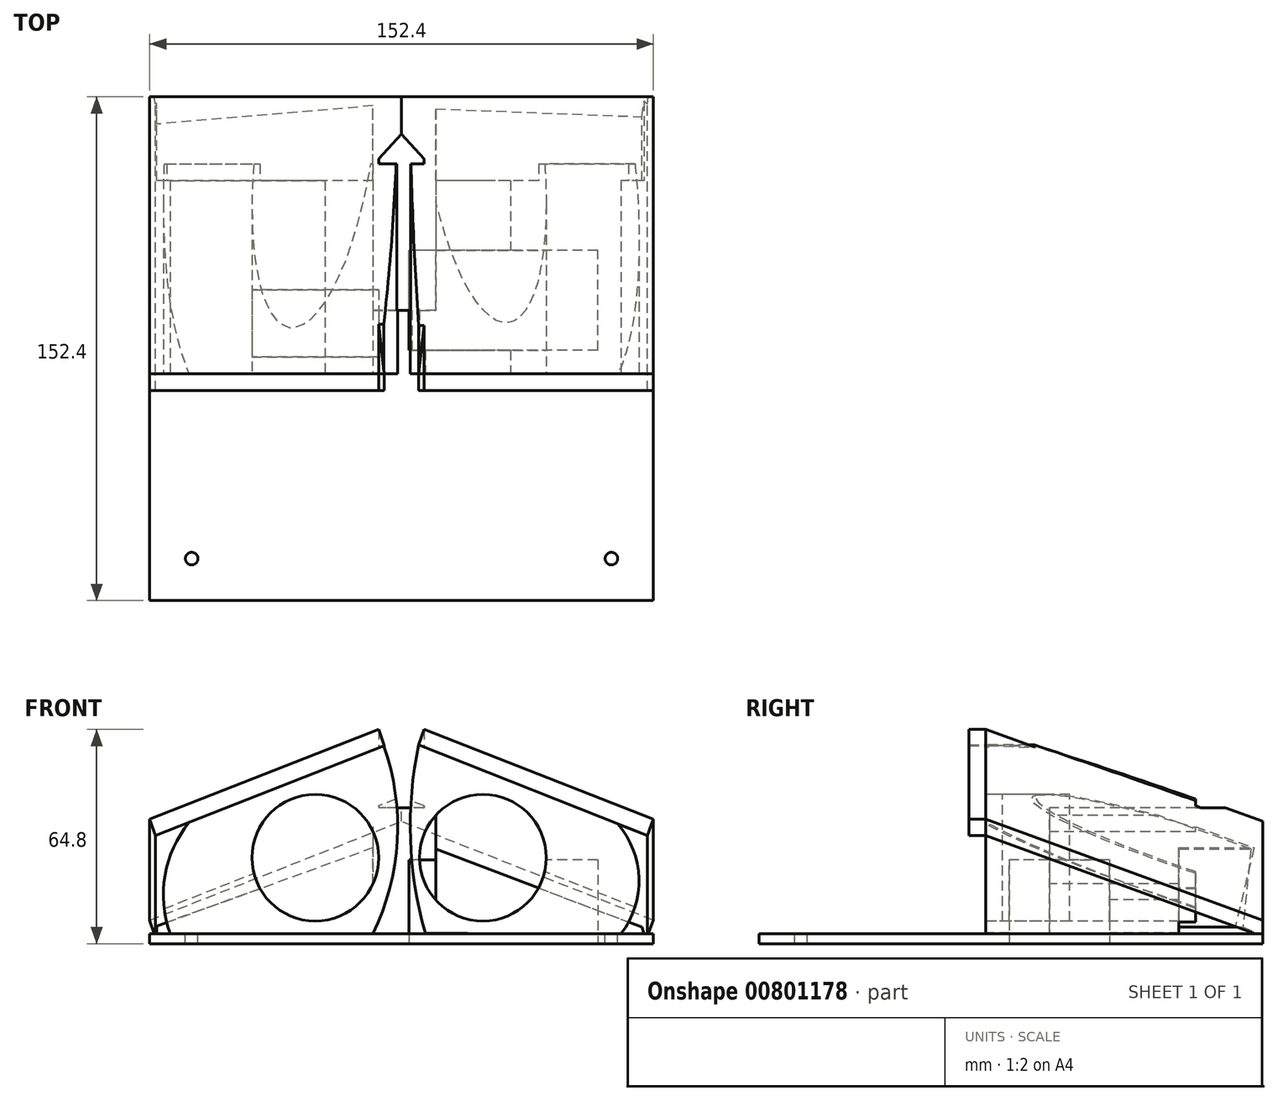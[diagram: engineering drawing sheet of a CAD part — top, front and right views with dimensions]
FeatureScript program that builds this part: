
annotation { "Feature Type Name" : "Feature", "Feature Type Description" : "" }
export const myFeature = defineFeature(function(context is Context, id is Id, definition is map)
    precondition{}
    {
        {
            var Q0;
            Q0=qCreatedBy(makeId("Top.planeOp"),FACE);
            var sketch = newSketch(context, id + "F0", { "sketchPlane" : qUnion([Q0])});
            skLineSegment(sketch, "E0.bottom", {"start": v(0, 0) * mm, "end": v(152.4, 0) * mm});
            skLineSegment(sketch, "E0.top", {"start": v(0, 152.4) * mm, "end": v(152.4, 152.4) * mm});
            skLineSegment(sketch, "E0.left", {"start": v(0, 0) * mm, "end": v(0, 152.4) * mm});
            skLineSegment(sketch, "E0.right", {"start": v(152.4, 0) * mm, "end": v(152.4, 152.4) * mm});
            skSolve(sketch);
        }
        {
            var Q0;
            Q0=makeQuery(id+"F0.imprint","IMPRINT",FACE,{"disambiguationData":[TD([[makeQuery(id+"F0.imprint","IMPRINT",EDGE,{"derivedFrom":sQuery(id+"F0.wireOp",EDGE,"E0.bottom")}),1.0]])]});
            extrude(context, id + "F1", {"entities" : qUnion([Q0]), "depth" : 3 * mm, "offsetDistance" : 25.4 * mm});
        }
        {
            var Q0;
            Q0=makeQuery(id+"F1.opExtrude","CAP_EDGE",EDGE,{"disambiguationData":[OSD([sQuery(id+"F0.wireOp",EDGE,"E0.top")])],"isStart":false});
            cPlane(context, id + "F2", {"entities" : qUnion([Q0]), "cplaneType" : CPlaneType.LINE_ANGLE, "offset" : 25.4 * mm, "angle" : 20 * degree, "oppositeDirection" : true, "width" : 152.4 * mm, "height" : 152.4 * mm});
        }
        {
            var Q0;
            Q0=qCreatedBy(id+"F2.planeOp",FACE);
            var sketch = newSketch(context, id + "F3", { "sketchPlane" : qUnion([Q0])});
            skLineSegment(sketch, "E1", {"start": v(-1.71, 54.15) * mm, "end": v(-70.98, 79.7) * mm});
            skLineSegment(sketch, "E2", {"start": v(-70.98, 79.7) * mm, "end": v(-69.27, 84.35) * mm});
            skLineSegment(sketch, "E3", {"start": v(-69.27, 84.35) * mm, "end": v(0, 58.8) * mm});
            skLineSegment(sketch, "E4", {"start": v(0, 58.8) * mm, "end": v(-1.71, 54.15) * mm});
            skLineSegment(sketch, "E5", {"start": v(0, 51.14) * mm, "end": v(-152.3, 51.14) * mm});
            skLineSegment(sketch, "E6", {"start": v(-76.15, 51.14) * mm, "end": v(-76.15, 93.23) * mm});
            skLineSegment(sketch, "E7.MirrorCS", {"start": v(-150.6, 54.15) * mm, "end": v(-81.32, 79.7) * mm});
            skLineSegment(sketch, "E8.MirrorCS", {"start": v(-83.04, 84.35) * mm, "end": v(-152.3, 58.8) * mm});
            skLineSegment(sketch, "E9.MirrorCS", {"start": v(-81.32, 79.7) * mm, "end": v(-83.04, 84.35) * mm});
            skLineSegment(sketch, "E10.MirrorCS", {"start": v(-152.3, 58.8) * mm, "end": v(-150.6, 54.15) * mm});
            skSolve(sketch);
        }
        {
            var Q0;
            Q0=makeQuery(id+"F3.imprint","IMPRINT",FACE,{"disambiguationData":[TD([[makeQuery(id+"F3.imprint","IMPRINT",EDGE,{"derivedFrom":sQuery(id+"F3.wireOp",EDGE,"E1")}),-1.0]])]});
            var Q1;
            Q1=makeQuery(id+"F3.imprint","IMPRINT",FACE,{"disambiguationData":[TD([[makeQuery(id+"F3.imprint","IMPRINT",EDGE,{"derivedFrom":sQuery(id+"F3.wireOp",EDGE,"E7.MirrorCS")}),1.0]])]});
            extrude(context, id + "F4", {"entities" : qUnion([Q0, Q1]), "operationType" : NewBodyOperationType.ADD, "oppositeDirection" : true, "depth" : 101.6 * mm, "offsetDistance" : 25.4 * mm});
        }
        {
            var Q0;
            Q0=makeQuery(id+"F1.opExtrude","SWEPT_FACE",FACE,{"disambiguationData":[OSD([sQuery(id+"F0.wireOp",EDGE,"E0.bottom")])]});
            cPlane(context, id + "F5", {"entities" : qUnion([Q0]), "cplaneType" : CPlaneType.OFFSET, "offset" : 68.58 * mm, "oppositeDirection" : true, "width" : 152.4 * mm, "height" : 152.4 * mm});
        }
        {
            var Q0;
            Q0=makeQuery(id+"F1.opExtrude","SWEPT_FACE",FACE,{"disambiguationData":[OSD([sQuery(id+"F0.wireOp",EDGE,"E0.top")])]});
            cPlane(context, id + "F6", {"entities" : qUnion([Q0]), "cplaneType" : CPlaneType.OFFSET, "offset" : 0 * mm, "width" : 152.4 * mm, "height" : 152.4 * mm});
        }
        {
            var Q0;
            Q0=qCreatedBy(id+"F6.planeOp",FACE);
            var sketch = newSketch(context, id + "F7", { "sketchPlane" : qUnion([Q0])});
            skLineSegment(sketch, "E11.bottom", {"start": v(-167.5, 48.25) * mm, "end": v(7.13, 48.25) * mm});
            skLineSegment(sketch, "E11.top", {"start": v(-167.5, -23.65) * mm, "end": v(7.13, -23.65) * mm});
            skLineSegment(sketch, "E11.left", {"start": v(-167.5, 48.25) * mm, "end": v(-167.5, -23.65) * mm});
            skLineSegment(sketch, "E11.right", {"start": v(7.13, 48.25) * mm, "end": v(7.13, -23.65) * mm});
            skSolve(sketch);
        }
        {
            var Q0;
            Q0=makeQuery(id+"F7.imprint","IMPRINT",FACE,{"disambiguationData":[TD([[makeQuery(id+"F7.imprint","IMPRINT",EDGE,{"derivedFrom":sQuery(id+"F7.wireOp",EDGE,"E11.bottom")}),-1.0]])]});
            extrude(context, id + "F8", {"entities" : qUnion([Q0]), "operationType" : NewBodyOperationType.REMOVE, "depth" : 25.4 * mm, "offsetDistance" : 25.4 * mm});
        }
        {
            var Q0;
            Q0=qCreatedBy(id+"F5.planeOp",FACE);
            var sketch = newSketch(context, id + "F9", { "sketchPlane" : qUnion([Q0])});
            skLineSegment(sketch, "E12.bottom", {"start": v(-28, 78.49) * mm, "end": v(162.26, 78.49) * mm});
            skLineSegment(sketch, "E12.top", {"start": v(-28, 8.9) * mm, "end": v(162.26, 8.9) * mm});
            skLineSegment(sketch, "E12.left", {"start": v(-28, 78.49) * mm, "end": v(-28, 8.9) * mm});
            skLineSegment(sketch, "E12.right", {"start": v(162.26, 78.49) * mm, "end": v(162.26, 8.9) * mm});
            skSolve(sketch);
        }
        {
            var Q0;
            Q0=makeQuery(id+"F9.imprint","IMPRINT",FACE,{"disambiguationData":[TD([[makeQuery(id+"F9.imprint","IMPRINT",EDGE,{"derivedFrom":sQuery(id+"F9.wireOp",EDGE,"E12.bottom")}),-1.0]])]});
            extrude(context, id + "F10", {"entities" : qUnion([Q0]), "operationType" : NewBodyOperationType.REMOVE, "depth" : 25.4 * mm, "offsetDistance" : 25.4 * mm});
        }
        {
            var Q0;
            Q0=qCreatedBy(id+"F5.planeOp",FACE);
            var sketch = newSketch(context, id + "F11", { "sketchPlane" : qUnion([Q0])});
            skCircle(sketch, "E13", {"center": v(50.1, 26.01) * mm, "radius": 19.17 * mm});
            skCircle(sketch, "E14", {"center": v(100.82, 26.01) * mm, "radius": 19.17 * mm});
            skArc(sketch, "E15", {"start": v(67.55, 2.96) * mm, "mid": v(74.9, 31.12) * mm, "end": v(70.85, 59.94) * mm});
            skArc(sketch, "E16", {"start": v(81.38, 60.1) * mm, "mid": v(78.93, 31.58) * mm, "end": v(83.35, 3.28) * mm});
            skArc(sketch, "E17", {"start": v(12.38, 37.21) * mm, "mid": v(4.68, 21) * mm, "end": v(6.13, 3.12) * mm});
            skArc(sketch, "E18", {"start": v(142.32, 2.63) * mm, "mid": v(148.07, 20) * mm, "end": v(141, 36.88) * mm});
            skLineSegment(sketch, "E19", {"start": v(6.13, 3.12) * mm, "end": v(67.55, 2.96) * mm});
            skLineSegment(sketch, "E20", {"start": v(83.35, 3.28) * mm, "end": v(142.32, 2.63) * mm});
            skLineSegment(sketch, "E21", {"start": v(81.38, 60.1) * mm, "end": v(141, 36.88) * mm});
            skLineSegment(sketch, "E22", {"start": v(70.85, 59.94) * mm, "end": v(12.38, 37.21) * mm});
            skSolve(sketch);
        }
        {
            var Q0;
            Q0=makeQuery(id+"F11.imprint","IMPRINT",FACE,{"disambiguationData":[TD([[makeQuery(id+"F11.imprint","IMPRINT",EDGE,{"derivedFrom":sQuery(id+"F11.wireOp",EDGE,"E13")}),-1.0]])]});
            var Q1;
            Q1=makeQuery(id+"F11.imprint","IMPRINT",FACE,{"disambiguationData":[TD([[makeQuery(id+"F11.imprint","IMPRINT",EDGE,{"derivedFrom":sQuery(id+"F11.wireOp",EDGE,"E14")}),-1.0]])]});
            extrude(context, id + "F12", {"entities" : qUnion([Q0, Q1]), "operationType" : NewBodyOperationType.ADD, "oppositeDirection" : true, "depth" : 63.5 * mm, "offsetDistance" : 25.4 * mm});
        }
        {
            var Q0;
            Q0=makeQuery(id+"F4.opExtrude","SWEPT_FACE",FACE,{"disambiguationData":[OSD([sQuery(id+"F3.wireOp",EDGE,"E8.MirrorCS")])]});
            var sketch = newSketch(context, id + "F13", { "sketchPlane" : qUnion([Q0])});
            skLineSegment(sketch, "E23.bottom", {"start": v(48.73, 42.28) * mm, "end": v(122.55, 42.28) * mm});
            skLineSegment(sketch, "E23.top", {"start": v(48.73, 140.78) * mm, "end": v(122.55, 140.78) * mm});
            skLineSegment(sketch, "E23.left", {"start": v(48.73, 42.28) * mm, "end": v(48.73, 140.78) * mm});
            skLineSegment(sketch, "E23.right", {"start": v(122.55, 42.28) * mm, "end": v(122.55, 140.78) * mm});
            skSolve(sketch);
        }
        {
            var Q0;
            Q0=makeQuery(id+"F4.opExtrude","SWEPT_FACE",FACE,{"disambiguationData":[OSD([sQuery(id+"F3.wireOp",EDGE,"E3")])]});
            var sketch = newSketch(context, id + "F14", { "sketchPlane" : qUnion([Q0])});
            skLineSegment(sketch, "E24.bottom", {"start": v(20.35, 140.78) * mm, "end": v(162.55, 140.78) * mm});
            skLineSegment(sketch, "E24.top", {"start": v(20.35, 0) * mm, "end": v(162.55, 0) * mm});
            skLineSegment(sketch, "E24.left", {"start": v(20.35, 140.78) * mm, "end": v(20.35, 0) * mm});
            skLineSegment(sketch, "E24.right", {"start": v(162.55, 140.78) * mm, "end": v(162.55, 0) * mm});
            skSolve(sketch);
        }
        {
            var Q0;
            Q0=makeQuery(id+"F19.boolean.opBoolean","MERGE",FACE,{"derivedFrom":[makeQuery(id+"F4.opExtrude","SWEPT_FACE",FACE,{"disambiguationData":[OSD([sQuery(id+"F3.wireOp",EDGE,"E8.MirrorCS")])]}),makeQuery(id+"F19.opExtrude","CAP_FACE",FACE,{"disambiguationData":[OSD([sQuery(id+"F13.wireOp",EDGE,"E23.bottom"),sQuery(id+"F13.wireOp",EDGE,"E23.top"),sQuery(id+"F13.wireOp",EDGE,"E23.left"),sQuery(id+"F13.wireOp",EDGE,"E23.right")])],"isStart":true})]});
            var sketch = newSketch(context, id + "F15", { "sketchPlane" : qUnion([Q0])});
            skLineSegment(sketch, "E25.bottom", {"start": v(92.17, 120.01) * mm, "end": v(2.78, 120.01) * mm});
            skLineSegment(sketch, "E25.top", {"start": v(92.17, 34.87) * mm, "end": v(2.78, 34.87) * mm});
            skLineSegment(sketch, "E25.left", {"start": v(92.17, 120.01) * mm, "end": v(92.17, 34.87) * mm});
            skLineSegment(sketch, "E25.right", {"start": v(2.78, 120.01) * mm, "end": v(2.78, 34.87) * mm});
            skSolve(sketch);
        }
        {
            var Q0;
            Q0=makeQuery(id+"F1.opExtrude","CAP_FACE",FACE,{"disambiguationData":[OSD([sQuery(id+"F0.wireOp",EDGE,"E0.bottom"),sQuery(id+"F0.wireOp",EDGE,"E0.top"),sQuery(id+"F0.wireOp",EDGE,"E0.left"),sQuery(id+"F0.wireOp",EDGE,"E0.right")])],"isStart":false});
            var sketch = newSketch(context, id + "F16", { "sketchPlane" : qUnion([Q0])});
            skLineSegment(sketch, "E26.bottom", {"start": v(67.57, 152.4) * mm, "end": v(86.52, 152.4) * mm});
            skLineSegment(sketch, "E26.top", {"start": v(67.57, 87.8) * mm, "end": v(86.52, 87.8) * mm});
            skLineSegment(sketch, "E26.left", {"start": v(67.57, 152.4) * mm, "end": v(67.57, 87.8) * mm});
            skLineSegment(sketch, "E26.right", {"start": v(86.52, 152.4) * mm, "end": v(86.52, 87.8) * mm});
            skSolve(sketch);
        }
        {
            var Q0;
            Q0 = qSketchRegion(id + "F16", true);
            extrude(context, id + "F17", {"entities" : qUnion([Q0]), "operationType" : NewBodyOperationType.ADD, "depth" : 38.1 * mm, "offsetDistance" : 25.4 * mm});
        }
        {
            var Q0;
            Q0 = qSketchRegion(id + "F14", true);
            extrude(context, id + "F18", {"entities" : qUnion([Q0]), "operationType" : NewBodyOperationType.REMOVE, "depth" : 25.4 * mm, "offsetDistance" : 25.4 * mm});
        }
        {
            var Q0;
            Q0 = qSketchRegion(id + "F13", true);
            extrude(context, id + "F19", {"entities" : qUnion([Q0]), "operationType" : NewBodyOperationType.REMOVE, "depth" : 25.4 * mm, "offsetDistance" : 25.4 * mm});
        }
        {
            var Q0;
            Q0 = qSketchRegion(id + "F15", true);
            extrude(context, id + "F20", {"entities" : qUnion([Q0]), "operationType" : NewBodyOperationType.REMOVE, "depth" : 25.4 * mm, "offsetDistance" : 25.4 * mm});
        }
        {
            var Q0;
            {var subQ7=makeQuery(id+"F4.opExtrude","SWEPT_FACE",FACE,{"disambiguationData":[OSD([sQuery(id+"F3.wireOp",EDGE,"E8.MirrorCS")])]});var subQ9=sQuery(id+"F16.wireOp",EDGE,"E26.right");var subQ10=sQuery(id+"F16.wireOp",EDGE,"E26.bottom");var subQ11=subQ7;Q0=makeQuery(id+"F20.boolean.opBoolean","MERGE",FACE,{"derivedFrom":[makeQuery(id+"F19.boolean.opBoolean","MERGE",FACE,{"derivedFrom":[makeQuery(id+"F17.boolean.opBoolean","SPLIT",FACE,{"disambiguationData":[TD([makeQuery(id+"F17.opExtrude","CAP_FACE",FACE,{"disambiguationData":[OSD([subQ10,sQuery(id+"F16.wireOp",EDGE,"E26.top"),sQuery(id+"F16.wireOp",EDGE,"E26.left"),subQ9])],"isStart":false})])],"derivedFrom":subQ11}),makeQuery(id+"F17.boolean.opBoolean","SPLIT",FACE,{"disambiguationData":[TD([makeQuery(id+"F1.opExtrude","SWEPT_FACE",FACE,{"disambiguationData":[OSD([sQuery(id+"F0.wireOp",EDGE,"E0.top")])]})])],"derivedFrom":subQ11}),makeQuery(id+"F19.opExtrude","CAP_FACE",FACE,{"disambiguationData":[OSD([sQuery(id+"F13.wireOp",EDGE,"E23.bottom"),sQuery(id+"F13.wireOp",EDGE,"E23.top"),sQuery(id+"F13.wireOp",EDGE,"E23.left"),sQuery(id+"F13.wireOp",EDGE,"E23.right")])],"isStart":true})]}),makeQuery(id+"F20.opExtrude","CAP_FACE",FACE,{"disambiguationData":[OSD([sQuery(id+"F15.wireOp",EDGE,"E25.bottom"),sQuery(id+"F15.wireOp",EDGE,"E25.top"),sQuery(id+"F15.wireOp",EDGE,"E25.left"),sQuery(id+"F15.wireOp",EDGE,"E25.right")])],"isStart":true})]});}
            var sketch = newSketch(context, id + "F21", { "sketchPlane" : qUnion([Q0])});
            skLineSegment(sketch, "E27.bottom", {"start": v(97.74, 106.36) * mm, "end": v(-10.12, 106.36) * mm});
            skLineSegment(sketch, "E27.top", {"start": v(97.74, 152.47) * mm, "end": v(-10.12, 152.47) * mm});
            skLineSegment(sketch, "E27.left", {"start": v(97.74, 106.36) * mm, "end": v(97.74, 152.47) * mm});
            skLineSegment(sketch, "E27.right", {"start": v(-10.12, 106.36) * mm, "end": v(-10.12, 152.47) * mm});
            skSolve(sketch);
        }
        {
            var Q0;
            Q0 = qSketchRegion(id + "F21", true);
            extrude(context, id + "F22", {"entities" : qUnion([Q0]), "operationType" : NewBodyOperationType.REMOVE, "depth" : 25.4 * mm, "offsetDistance" : 25.4 * mm});
        }
        {
            var Q0;
            Q0=makeQuery(id+"F11.imprint","IMPRINT",FACE,{"disambiguationData":[TD([[makeQuery(id+"F11.imprint","IMPRINT",EDGE,{"derivedFrom":sQuery(id+"F11.wireOp",EDGE,"E13")}),1.0]])]});
            extrude(context, id + "F23", {"entities" : qUnion([Q0]), "oppositeDirection" : true, "depth" : 25.4 * mm, "offsetDistance" : 25.4 * mm});
        }
        {
            var Q0;
            Q0=makeQuery(id+"F11.imprint","IMPRINT",FACE,{"disambiguationData":[TD([[makeQuery(id+"F11.imprint","IMPRINT",EDGE,{"derivedFrom":sQuery(id+"F11.wireOp",EDGE,"E13")}),1.0]])]});
            extrude(context, id + "F24", {"entities" : qUnion([Q0]), "operationType" : NewBodyOperationType.REMOVE, "oppositeDirection" : true, "depth" : 5.08 * mm, "offsetDistance" : 25.4 * mm});
        }
        {
            var Q0;
            Q0=makeQuery(id+"F12.boolean.opBoolean","MERGE",FACE,{"derivedFrom":[makeQuery(id+"F10.boolean.opBoolean","COPY",FACE,{"disambiguationData":[TD([makeQuery(id+"F4.opExtrude","SWEPT_FACE",FACE,{"disambiguationData":[OSD([sQuery(id+"F3.wireOp",EDGE,"E1")])]})])],"derivedFrom":makeQuery(id+"F10.opExtrude","CAP_FACE",FACE,{"disambiguationData":[OSD([sQuery(id+"F9.wireOp",EDGE,"E12.bottom"),sQuery(id+"F9.wireOp",EDGE,"E12.top"),sQuery(id+"F9.wireOp",EDGE,"E12.left"),sQuery(id+"F9.wireOp",EDGE,"E12.right")])],"isStart":true})}),makeQuery(id+"F12.opExtrude","CAP_FACE",FACE,{"disambiguationData":[OSD([sQuery(id+"F11.wireOp",EDGE,"E13"),sQuery(id+"F11.wireOp",EDGE,"E15"),sQuery(id+"F11.wireOp",EDGE,"E17"),sQuery(id+"F11.wireOp",EDGE,"E19"),sQuery(id+"F11.wireOp",EDGE,"E22")])],"isStart":true})]});
            var sketch = newSketch(context, id + "F25", { "sketchPlane" : qUnion([Q0])});
            skLineSegment(sketch, "E28", {"start": v(1.71, 32.67) * mm, "end": v(0, 37.62) * mm});
            skLineSegment(sketch, "E29", {"start": v(0, 37.62) * mm, "end": v(69.27, 64.8) * mm});
            skLineSegment(sketch, "E30", {"start": v(69.27, 64.8) * mm, "end": v(70.98, 59.85) * mm});
            skLineSegment(sketch, "E31", {"start": v(70.98, 59.85) * mm, "end": v(1.71, 32.67) * mm});
            skSolve(sketch);
        }
        {
            var Q0;
            {var subQ1=sQuery(id+"F25.wireOp",EDGE,"E28");Q0=makeQuery(id+"F25.imprint","IMPRINT",FACE,{"disambiguationData":[TD([[makeQuery(id+"F25.imprint","IMPRINT",EDGE,{"derivedFrom":subQ1}),1.0]])]});}
            extrude(context, id + "F26", {"entities" : qUnion([Q0]), "operationType" : NewBodyOperationType.ADD, "depth" : 5.08 * mm, "offsetDistance" : 25.4 * mm});
        }
        {
            var Q0;
            Q0=makeQuery(id+"F12.boolean.opBoolean","MERGE",FACE,{"derivedFrom":[makeQuery(id+"F10.boolean.opBoolean","COPY",FACE,{"disambiguationData":[TD([makeQuery(id+"F4.opExtrude","SWEPT_FACE",FACE,{"disambiguationData":[OSD([sQuery(id+"F3.wireOp",EDGE,"E7.MirrorCS")])]})])],"derivedFrom":makeQuery(id+"F10.opExtrude","CAP_FACE",FACE,{"disambiguationData":[OSD([sQuery(id+"F9.wireOp",EDGE,"E12.bottom"),sQuery(id+"F9.wireOp",EDGE,"E12.top"),sQuery(id+"F9.wireOp",EDGE,"E12.left"),sQuery(id+"F9.wireOp",EDGE,"E12.right")])],"isStart":true})}),makeQuery(id+"F12.opExtrude","CAP_FACE",FACE,{"disambiguationData":[OSD([sQuery(id+"F11.wireOp",EDGE,"E14"),sQuery(id+"F11.wireOp",EDGE,"E16"),sQuery(id+"F11.wireOp",EDGE,"E18"),sQuery(id+"F11.wireOp",EDGE,"E20"),sQuery(id+"F11.wireOp",EDGE,"E21")])],"isStart":true})]});
            var sketch = newSketch(context, id + "F27", { "sketchPlane" : qUnion([Q0])});
            skLineSegment(sketch, "E32", {"start": v(81.4, 60.1) * mm, "end": v(83.04, 64.8) * mm});
            skLineSegment(sketch, "E33", {"start": v(83.04, 64.8) * mm, "end": v(152.3, 37.62) * mm});
            skLineSegment(sketch, "E34", {"start": v(152.3, 37.62) * mm, "end": v(150.6, 32.67) * mm});
            skLineSegment(sketch, "E35", {"start": v(150.6, 32.67) * mm, "end": v(81.4, 60.1) * mm});
            skSolve(sketch);
        }
        {
            var Q0;
            Q0=makeQuery(id+"F27.imprint","IMPRINT",FACE,{"disambiguationData":[TD([[makeQuery(id+"F27.imprint","IMPRINT",EDGE,{"derivedFrom":sQuery(id+"F27.wireOp",EDGE,"E32")}),-1.0]])]});
            extrude(context, id + "F28", {"entities" : qUnion([Q0]), "operationType" : NewBodyOperationType.ADD, "depth" : 5.08 * mm, "offsetDistance" : 25.4 * mm});
        }
        {
            var Q0;
            Q0=makeQuery(id+"F17.boolean.opBoolean","MERGE",FACE,{"derivedFrom":[makeQuery(id+"F8.boolean.opBoolean","MERGE",FACE,{"derivedFrom":[makeQuery(id+"F1.opExtrude","SWEPT_FACE",FACE,{"disambiguationData":[OSD([sQuery(id+"F0.wireOp",EDGE,"E0.top")])]}),makeQuery(id+"F8.opExtrude","CAP_FACE",FACE,{"disambiguationData":[OSD([sQuery(id+"F7.wireOp",EDGE,"E11.bottom"),sQuery(id+"F7.wireOp",EDGE,"E11.top"),sQuery(id+"F7.wireOp",EDGE,"E11.left"),sQuery(id+"F7.wireOp",EDGE,"E11.right")])],"isStart":true})]}),makeQuery(id+"F17.opExtrude","SWEPT_FACE",FACE,{"disambiguationData":[OSD([sQuery(id+"F16.wireOp",EDGE,"E26.bottom")])]})]});
            var sketch = newSketch(context, id + "F29", { "sketchPlane" : qUnion([Q0])});
            skLineSegment(sketch, "E36", {"start": v(-150.11, 1.52) * mm, "end": v(-148.95, 5) * mm});
            skLineSegment(sketch, "E37", {"start": v(-148.95, 5) * mm, "end": v(-76.78, 32.31) * mm});
            skLineSegment(sketch, "E38", {"start": v(-76.78, 32.31) * mm, "end": v(-2.12, 5.33) * mm});
            skLineSegment(sketch, "E39", {"start": v(-2.12, 5.33) * mm, "end": v(-2.12, 1.36) * mm});
            skLineSegment(sketch, "E40", {"start": v(-2.12, 1.36) * mm, "end": v(-150.11, 1.52) * mm});
            skSolve(sketch);
        }
        {
            var Q0;
            Q0 = qSketchRegion(id + "F29", true);
            extrude(context, id + "F30", {"entities" : qUnion([Q0]), "operationType" : NewBodyOperationType.ADD, "oppositeDirection" : true, "depth" : 25.4 * mm, "offsetDistance" : 25.4 * mm});
        }
        {
            var Q0;
            Q0=makeQuery(id+"F1.opExtrude","CAP_FACE",FACE,{"disambiguationData":[OSD([sQuery(id+"F0.wireOp",EDGE,"E0.bottom"),sQuery(id+"F0.wireOp",EDGE,"E0.top"),sQuery(id+"F0.wireOp",EDGE,"E0.left"),sQuery(id+"F0.wireOp",EDGE,"E0.right")])],"isStart":true});
            var sketch = newSketch(context, id + "F31", { "sketchPlane" : qUnion([Q0])});
            skLineSegment(sketch, "E41.bottom", {"start": v(135.54, -75.7) * mm, "end": v(78.4, -75.7) * mm});
            skLineSegment(sketch, "E41.top", {"start": v(135.54, -105.97) * mm, "end": v(78.4, -105.97) * mm});
            skLineSegment(sketch, "E41.left", {"start": v(135.54, -75.7) * mm, "end": v(135.54, -105.97) * mm});
            skLineSegment(sketch, "E41.right", {"start": v(78.4, -75.7) * mm, "end": v(78.4, -105.97) * mm});
            skSolve(sketch);
        }
        {
            var Q0;
            Q0=makeQuery(id+"F31.imprint","IMPRINT",FACE,{"disambiguationData":[TD([[makeQuery(id+"F31.imprint","IMPRINT",EDGE,{"derivedFrom":sQuery(id+"F31.wireOp",EDGE,"E41.bottom")}),1.0]])]});
            extrude(context, id + "F32", {"entities" : qUnion([Q0]), "operationType" : NewBodyOperationType.REMOVE, "oppositeDirection" : true, "depth" : 25.4 * mm, "offsetDistance" : 25.4 * mm});
        }
        {
            var Q0;
            {var subQ8=sQuery(id+"F0.wireOp",EDGE,"E0.left");var subQ9=sQuery(id+"F0.wireOp",EDGE,"E0.top");var subQ11=sQuery(id+"F0.wireOp",EDGE,"E0.bottom");var subQ17=sQuery(id+"F0.wireOp",EDGE,"E0.right");Q0=makeQuery(id+"F32.boolean.opBoolean","SPLIT",FACE,{"disambiguationData":[TD([makeQuery(id+"F1.opExtrude","SWEPT_FACE",FACE,{"disambiguationData":[OSD([subQ11])]})])],"derivedFrom":makeQuery(id+"F1.opExtrude","CAP_FACE",FACE,{"disambiguationData":[OSD([subQ11,subQ9,subQ8,subQ17])],"isStart":false})});}
            var sketch = newSketch(context, id + "F33", { "sketchPlane" : qUnion([Q0])});
            skCircle(sketch, "E42", {"center": v(12.7, 12.7) * mm, "radius": 1.9 * mm});
            skCircle(sketch, "E43", {"center": v(139.7, 12.7) * mm, "radius": 1.9 * mm});
            skSolve(sketch);
        }
        {
            var Q0;
            Q0=makeQuery(id+"F33.imprint","IMPRINT",FACE,{"disambiguationData":[TD([[makeQuery(id+"F33.imprint","IMPRINT",EDGE,{"derivedFrom":sQuery(id+"F33.wireOp",EDGE,"E42")}),1.0]])]});
            var Q1;
            Q1=makeQuery(id+"F33.imprint","IMPRINT",FACE,{"disambiguationData":[TD([[makeQuery(id+"F33.imprint","IMPRINT",EDGE,{"derivedFrom":sQuery(id+"F33.wireOp",EDGE,"E43")}),1.0]])]});
            extrude(context, id + "F34", {"entities" : qUnion([Q0, Q1]), "operationType" : NewBodyOperationType.REMOVE, "oppositeDirection" : true, "depth" : 25.4 * mm, "offsetDistance" : 25.4 * mm});
        }
    });
